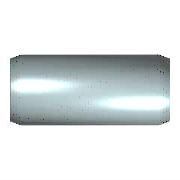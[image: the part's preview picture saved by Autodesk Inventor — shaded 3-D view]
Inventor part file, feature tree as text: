
AUTODESK INVENTOR PART (.ipt)
format: ipt  version: 2023.3 (Build 273359000, 359)  size: 113,152 bytes
history: native  units: mm (DEFAULTED — no unit token found)
features: extrude x1, chamfer x1, sketch x1
ambient origin geometry x8: Origin, YZ Plane, XZ Plane, XY Plane, X Axis, Y Axis, Z Axis, Center Point
bodies: Solid1 (feature_tree)
feature tree (3):
  extrude  "Körper"  Depth=16.0mm
  chamfer  "Skizze2"  [1 undecoded]
  sketch  "Skizze"  dims[d1=2.0mm d2=16.0mm d3=0.0mm d4=0.35mm d5=15.0deg d8=0.35mm d9=15.0deg d11=0.35mm d12=0.35mm d13=0.0mm d15=0.0mm d16=0.0mm]
note: 1 required parameter value undecoded (feature->parameter linkage not recoverable at this tier; creation-order binding heuristic only, values carry confidence <= 0.55)
